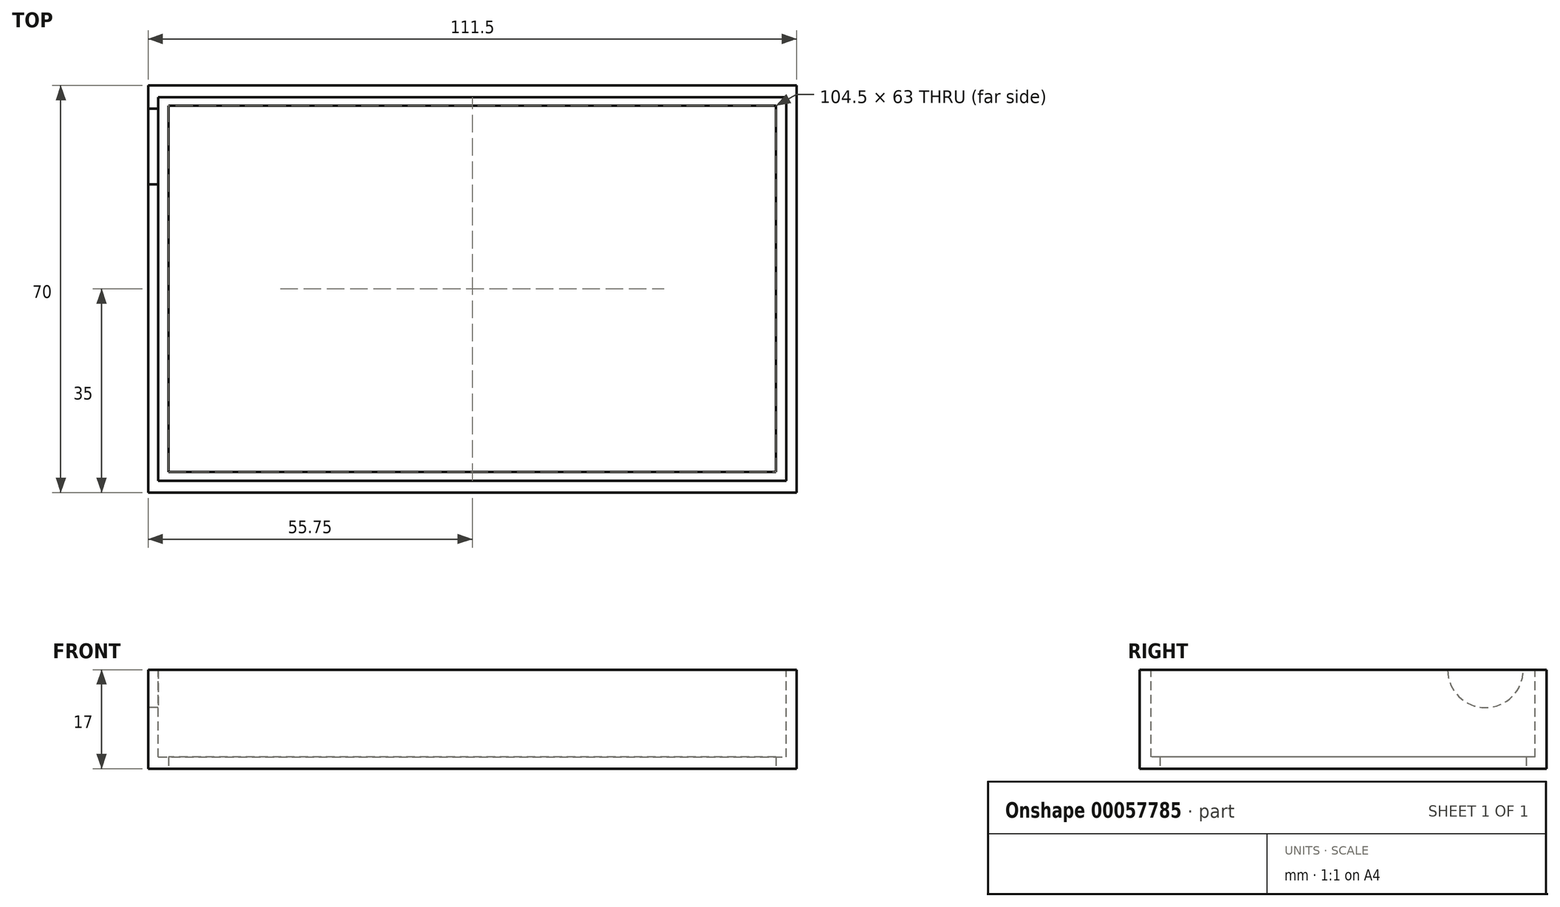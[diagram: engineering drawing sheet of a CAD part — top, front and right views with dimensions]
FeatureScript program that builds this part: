
annotation { "Feature Type Name" : "Feature", "Feature Type Description" : "" }
export const myFeature = defineFeature(function(context is Context, id is Id, definition is map)
    precondition{}
    {
        {
            var Q0;
            Q0=qCreatedBy(makeId("Top.planeOp"),FACE);
            var sketch = newSketch(context, id + "F0", { "sketchPlane" : qUnion([Q0])});
            skLineSegment(sketch, "E0.bottom", {"start": v(0, 0) * mm, "end": v(111.5, 0) * mm});
            skLineSegment(sketch, "E0.top", {"start": v(0, 70) * mm, "end": v(111.5, 70) * mm});
            skLineSegment(sketch, "E0.left", {"start": v(0, 0) * mm, "end": v(0, 70) * mm});
            skLineSegment(sketch, "E0.right", {"start": v(111.5, 0) * mm, "end": v(111.5, 70) * mm});
            skSolve(sketch);
        }
        {
            var Q0;
            Q0 = qSketchRegion(id + "F0", true);
            extrude(context, id + "F1", {"entities" : qUnion([Q0]), "depth" : 17 * mm});
        }
        {
            var Q0;
            Q0=makeQuery(id+"F1.opExtrude","CAP_FACE",FACE,{"disambiguationData":[OSD([sQuery(id+"F0.wireOp",EDGE,"E0.bottom"),sQuery(id+"F0.wireOp",EDGE,"E0.top"),sQuery(id+"F0.wireOp",EDGE,"E0.left"),sQuery(id+"F0.wireOp",EDGE,"E0.right")])],"isStart":false});
            var sketch = newSketch(context, id + "F2", { "sketchPlane" : qUnion([Q0])});
            skLineSegment(sketch, "E1", {"start": v(55.75, 70) * mm, "end": v(55.75, 0) * mm, "construction": true});
            skPoint(sketch, "E2.orphan", {"position": v(0, 35) * mm});
            skPoint(sketch, "E3.end.orphan", {"position": v(111.5, 35) * mm});
            skLineSegment(sketch, "E4", {"start": v(0, 35) * mm, "end": v(111.5, 35) * mm, "construction": true});
            skLineSegment(sketch, "E5.bottom", {"start": v(1.75, 68) * mm, "end": v(109.75, 68) * mm, "construction": true});
            skLineSegment(sketch, "E5.top", {"start": v(1.75, 2) * mm, "end": v(109.75, 2) * mm, "construction": true});
            skLineSegment(sketch, "E5.left", {"start": v(1.75, 68) * mm, "end": v(1.75, 2) * mm, "construction": true});
            skLineSegment(sketch, "E5.right", {"start": v(109.75, 68) * mm, "end": v(109.75, 2) * mm, "construction": true});
            skLineSegment(sketch, "E6.bottom", {"start": v(1.75, 68) * mm, "end": v(109.75, 68) * mm});
            skLineSegment(sketch, "E6.top", {"start": v(1.75, 2) * mm, "end": v(109.75, 2) * mm});
            skLineSegment(sketch, "E6.left", {"start": v(1.75, 68) * mm, "end": v(1.75, 2) * mm});
            skLineSegment(sketch, "E6.right", {"start": v(109.75, 68) * mm, "end": v(109.75, 2) * mm});
            skSolve(sketch);
        }
        {
            var Q0;
            Q0 = qSketchRegion(id + "F2", true);
            extrude(context, id + "F3", {"entities" : qUnion([Q0]), "operationType" : NewBodyOperationType.REMOVE, "oppositeDirection" : true, "depth" : 15 * mm});
        }
        {
            var Q0;
            Q0=makeQuery(id+"F1.opExtrude","CAP_FACE",FACE,{"disambiguationData":[OSD([sQuery(id+"F0.wireOp",EDGE,"E0.bottom"),sQuery(id+"F0.wireOp",EDGE,"E0.top"),sQuery(id+"F0.wireOp",EDGE,"E0.left"),sQuery(id+"F0.wireOp",EDGE,"E0.right")])],"isStart":true});
            var sketch = newSketch(context, id + "F4", { "sketchPlane" : qUnion([Q0])});
            skLineSegment(sketch, "E7.0", {"start": v(3.5, -3.5) * mm, "end": v(108, -3.5) * mm});
            skLineSegment(sketch, "E7.1", {"start": v(3.5, -3.5) * mm, "end": v(3.5, -66.5) * mm});
            skLineSegment(sketch, "E7.2", {"start": v(3.5, -66.5) * mm, "end": v(108, -66.5) * mm});
            skLineSegment(sketch, "E7.3", {"start": v(108, -3.5) * mm, "end": v(108, -66.5) * mm});
            skSolve(sketch);
        }
        {
            var Q0;
            Q0 = qSketchRegion(id + "F4", true);
            extrude(context, id + "F5", {"entities" : qUnion([Q0]), "operationType" : NewBodyOperationType.REMOVE, "endBound" : BoundingType.THROUGH_ALL, "oppositeDirection" : true, "depth" : 25 * mm});
        }
        {
            var Q0;
            Q0=makeQuery(id+"F1.opExtrude","SWEPT_FACE",FACE,{"disambiguationData":[OSD([sQuery(id+"F0.wireOp",EDGE,"E0.left")])]});
            var sketch = newSketch(context, id + "F6", { "sketchPlane" : qUnion([Q0])});
            skCircle(sketch, "E8", {"center": v(-59.5, 17) * mm, "radius": 6.5 * mm});
            skSolve(sketch);
        }
        {
            var Q0;
            {var subQ0=sQuery(id+"F6.wireOp",EDGE,"E8");var subQ1=makeQuery(id+"F1.opExtrude","CAP_EDGE",EDGE,{"disambiguationData":[OSD([sQuery(id+"F0.wireOp",EDGE,"E0.left")])],"isStart":false});var subQ2=makeQuery(id+"F6.imprint","INTERSECT",VERTEX,{"disambiguationData":[OD(0.0)],"derivedFrom":[subQ1,subQ0]});Q0=makeQuery(id+"F6.imprint","IMPRINT",FACE,{"disambiguationData":[TD([[makeQuery(id+"F6.imprint","IMPRINT",EDGE,{"disambiguationData":[TD([[subQ2,1.0]])],"derivedFrom":subQ0}),1.0]])]});}
            extrude(context, id + "F7", {"entities" : qUnion([Q0]), "operationType" : NewBodyOperationType.REMOVE, "endBound" : BoundingType.UP_TO_NEXT, "oppositeDirection" : true, "depth" : 25 * mm});
        }
    });
